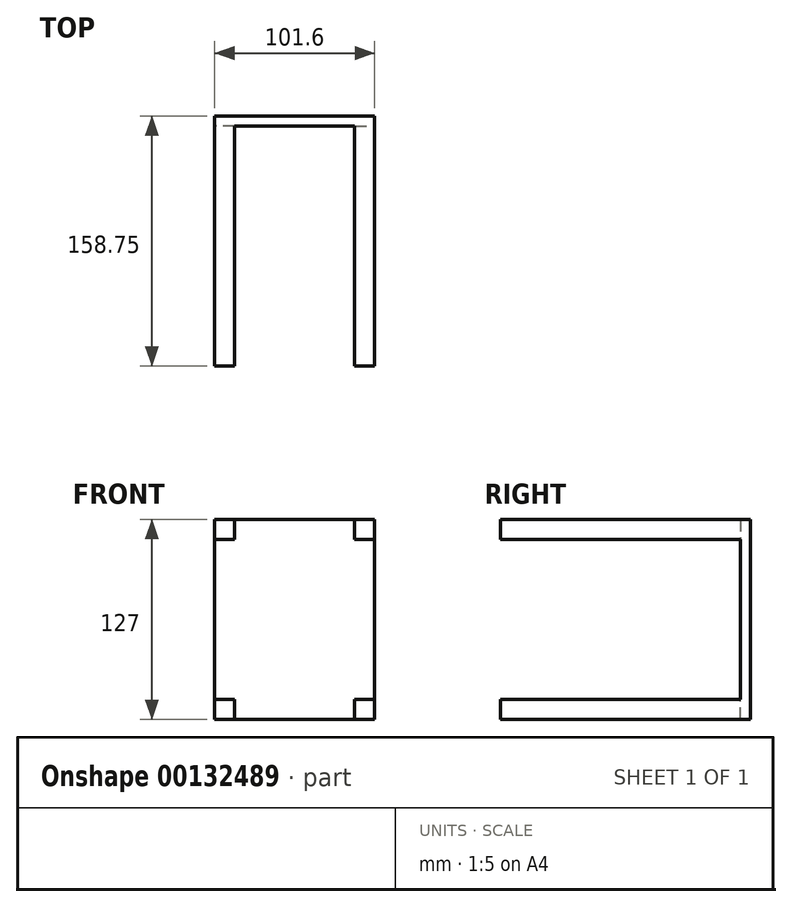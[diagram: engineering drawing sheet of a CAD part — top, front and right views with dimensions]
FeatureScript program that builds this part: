
annotation { "Feature Type Name" : "Feature", "Feature Type Description" : "" }
export const myFeature = defineFeature(function(context is Context, id is Id, definition is map)
    precondition{}
    {
        {
            var Q0;
            Q0=qCreatedBy(makeId("Front.planeOp"),FACE);
            var sketch = newSketch(context, id + "F0", { "sketchPlane" : qUnion([Q0])});
            skLineSegment(sketch, "E0.bottom", {"start": v(-50.8, 63.5) * mm, "end": v(50.8, 63.5) * mm});
            skLineSegment(sketch, "E0.top", {"start": v(-50.8, -63.5) * mm, "end": v(50.8, -63.5) * mm});
            skLineSegment(sketch, "E0.left", {"start": v(-50.8, 63.5) * mm, "end": v(-50.8, -63.5) * mm});
            skLineSegment(sketch, "E0.right", {"start": v(50.8, 63.5) * mm, "end": v(50.8, -63.5) * mm});
            skPoint(sketch, "E0.middle", {"position": v(0, 0) * mm});
            skSolve(sketch);
        }
        {
            var Q0;
            Q0=makeQuery(id+"F0.imprint","IMPRINT",FACE,{"disambiguationData":[TD([[makeQuery(id+"F0.imprint","IMPRINT",EDGE,{"derivedFrom":sQuery(id+"F0.wireOp",EDGE,"E0.bottom")}),-1.0]])]});
            extrude(context, id + "F1", {"entities" : qUnion([Q0]), "depth" : 6.35 * mm});
        }
        {
            var Q0;
            Q0=makeQuery(id+"F1.opExtrude","CAP_FACE",FACE,{"disambiguationData":[OSD([sQuery(id+"F0.wireOp",EDGE,"E0.bottom"),sQuery(id+"F0.wireOp",EDGE,"E0.top"),sQuery(id+"F0.wireOp",EDGE,"E0.left"),sQuery(id+"F0.wireOp",EDGE,"E0.right")])],"isStart":false});
            var sketch = newSketch(context, id + "F2", { "sketchPlane" : qUnion([Q0])});
            skLineSegment(sketch, "E1", {"start": v(-38.1, 63.5) * mm, "end": v(-38.1, 50.8) * mm});
            skLineSegment(sketch, "E2", {"start": v(-38.1, 50.8) * mm, "end": v(-50.8, 50.8) * mm});
            skLineSegment(sketch, "E3", {"start": v(-50.8, 50.8) * mm, "end": v(-50.8, 63.5) * mm});
            skLineSegment(sketch, "E4", {"start": v(-50.8, 63.5) * mm, "end": v(-38.1, 63.5) * mm});
            skLineSegment(sketch, "E5", {"start": v(38.1, 63.5) * mm, "end": v(38.1, 50.8) * mm});
            skLineSegment(sketch, "E6", {"start": v(38.1, 50.8) * mm, "end": v(50.8, 50.8) * mm});
            skLineSegment(sketch, "E7", {"start": v(50.8, 50.8) * mm, "end": v(50.8, 63.5) * mm});
            skLineSegment(sketch, "E8", {"start": v(50.8, 63.5) * mm, "end": v(38.1, 63.37) * mm});
            skLineSegment(sketch, "E9", {"start": v(-50.8, -50.8) * mm, "end": v(-38.1, -50.8) * mm});
            skLineSegment(sketch, "E10", {"start": v(-38.1, -50.8) * mm, "end": v(-38.1, -63.5) * mm});
            skLineSegment(sketch, "E11", {"start": v(-38.1, -63.5) * mm, "end": v(-50.8, -63.5) * mm});
            skLineSegment(sketch, "E12", {"start": v(-50.8, -63.5) * mm, "end": v(-50.8, -50.8) * mm});
            skLineSegment(sketch, "E13", {"start": v(50.8, -63.5) * mm, "end": v(38.1, -63.5) * mm});
            skLineSegment(sketch, "E14", {"start": v(38.1, -63.5) * mm, "end": v(38.1, -50.8) * mm});
            skLineSegment(sketch, "E15", {"start": v(38.1, -50.8) * mm, "end": v(50.8, -50.8) * mm});
            skLineSegment(sketch, "E16", {"start": v(50.8, -50.8) * mm, "end": v(50.8, -63.5) * mm});
            skSolve(sketch);
        }
        {
            var Q0;
            Q0 = qSketchRegion(id + "F2", true);
            var Q1;
            {var subQ0=sQuery(id+"F2.wireOp",EDGE,"E5");Q1=makeQuery(id+"F2.imprint","IMPRINT",FACE,{"disambiguationData":[TD([[makeQuery(id+"F2.imprint","IMPRINT",EDGE,{"derivedFrom":subQ0}),1.0]])]});}
            extrude(context, id + "F3", {"entities" : qUnion([Q0, Q1]), "operationType" : NewBodyOperationType.ADD, "depth" : 152.4 * mm});
        }
    });
